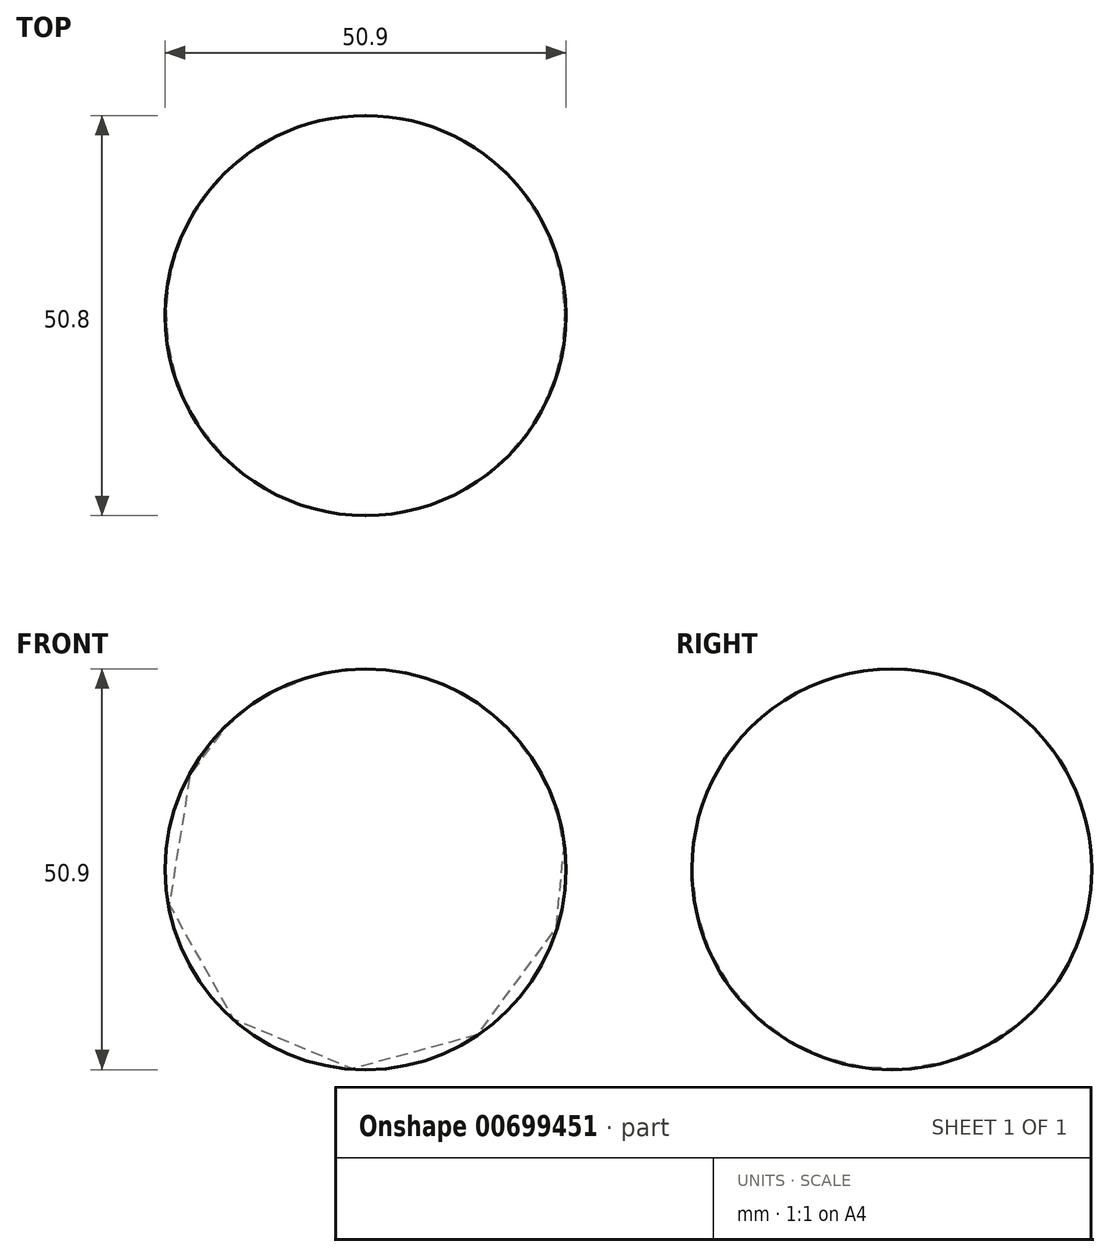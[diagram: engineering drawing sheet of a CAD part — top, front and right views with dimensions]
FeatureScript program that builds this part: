
annotation { "Feature Type Name" : "Feature", "Feature Type Description" : "" }
export const myFeature = defineFeature(function(context is Context, id is Id, definition is map)
    precondition{}
    {
        {
            var Q0;
            Q0=qCreatedBy(makeId("Top.planeOp"),FACE);
            var sketch = newSketch(context, id + "F0", { "sketchPlane" : qUnion([Q0])});
            skLineSegment(sketch, "E0", {"start": v(0, 0) * mm, "end": v(0, 50.8) * mm});
            skArc(sketch, "E1", {"start": v(0, 50.8) * mm, "mid": v(-25.45, 25.4) * mm, "end": v(0, 0) * mm});
            skSolve(sketch);
        }
        {
            var Q0;
            Q0=makeQuery(id+"F0.imprint","IMPRINT",FACE,{"disambiguationData":[TD([[makeQuery(id+"F0.imprint","IMPRINT",EDGE,{"derivedFrom":sQuery(id+"F0.wireOp",EDGE,"E0")}),1.0]])]});
            var Q1;
            Q1=sQuery(id+"F0.wireOp",EDGE,"E0");
            revolve(context, id + "F1", {"entities" : qUnion([Q0]), "axis" : qUnion([Q1]), "revolveType" : RevolveType.FULL});
        }
    });
